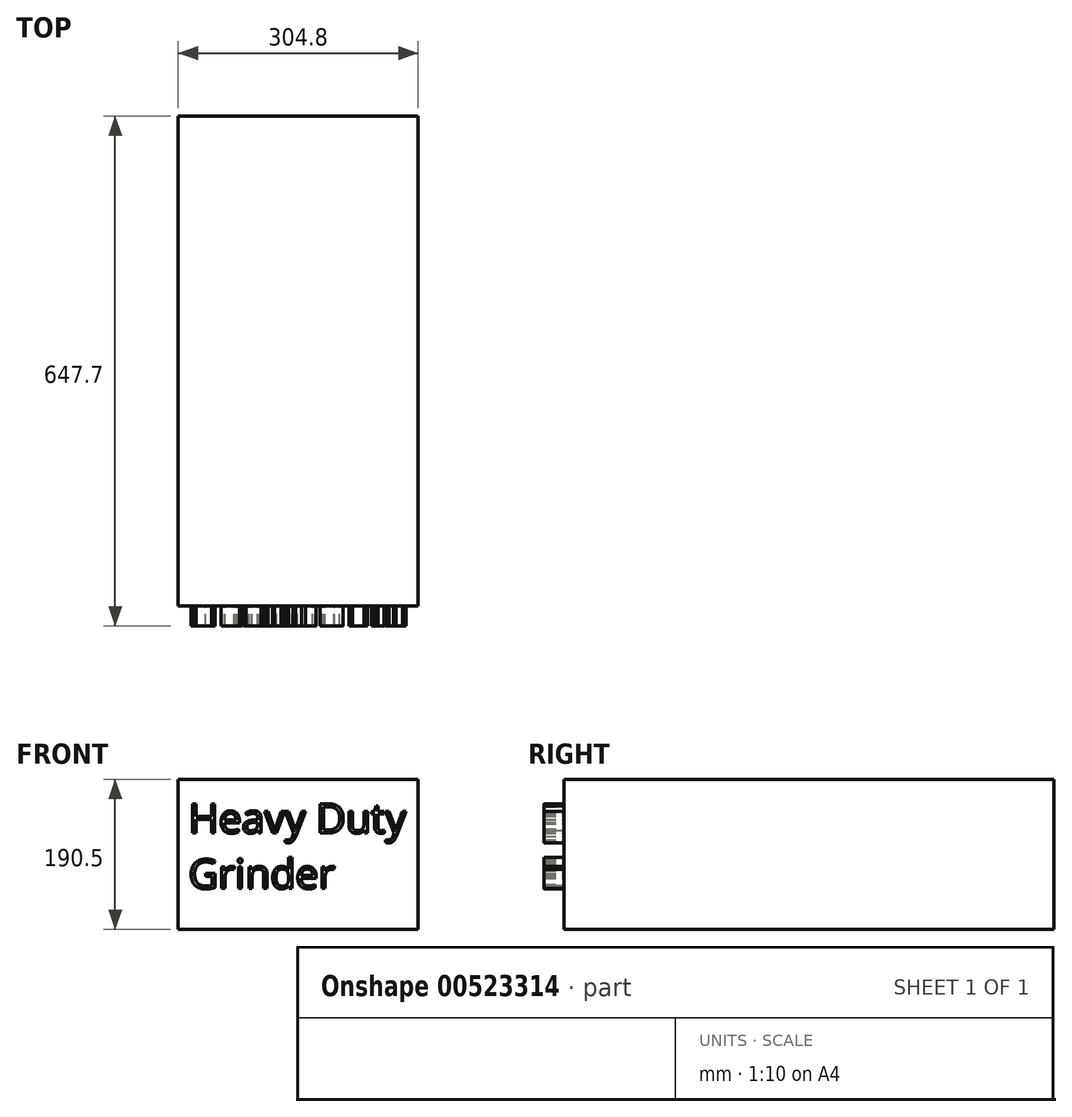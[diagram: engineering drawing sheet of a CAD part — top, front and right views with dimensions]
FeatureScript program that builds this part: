
annotation { "Feature Type Name" : "Feature", "Feature Type Description" : "" }
export const myFeature = defineFeature(function(context is Context, id is Id, definition is map)
    precondition{}
    {
        {
            var Q0;
            Q0=qCreatedBy(makeId("Front.planeOp"),FACE);
            var sketch = newSketch(context, id + "F0", { "sketchPlane" : qUnion([Q0])});
            skLineSegment(sketch, "E0.bottom", {"start": v(152.4, 95.25) * mm, "end": v(-152.4, 95.25) * mm});
            skLineSegment(sketch, "E0.top", {"start": v(152.4, -95.25) * mm, "end": v(-152.4, -95.25) * mm});
            skLineSegment(sketch, "E0.left", {"start": v(152.4, 95.25) * mm, "end": v(152.4, -95.25) * mm});
            skLineSegment(sketch, "E0.right", {"start": v(-152.4, 95.25) * mm, "end": v(-152.4, -95.25) * mm});
            skPoint(sketch, "E0.middle", {"position": v(0, 0) * mm});
            skSolve(sketch);
        }
        {
            var Q0;
            Q0=makeQuery(id+"F0.imprint","IMPRINT",FACE,{"disambiguationData":[TD([[makeQuery(id+"F0.imprint","IMPRINT",EDGE,{"derivedFrom":sQuery(id+"F0.wireOp",EDGE,"E0.bottom")}),1.0]])]});
            extrude(context, id + "F1", {"entities" : qUnion([Q0]), "depth" : 622.3 * mm, "offsetDistance" : 25.4 * mm});
        }
        {
            var Q0;
            Q0=makeQuery(id+"F1.opExtrude","CAP_FACE",FACE,{"disambiguationData":[OSD([sQuery(id+"F0.wireOp",EDGE,"E0.bottom"),sQuery(id+"F0.wireOp",EDGE,"E0.top"),sQuery(id+"F0.wireOp",EDGE,"E0.left"),sQuery(id+"F0.wireOp",EDGE,"E0.right")])],"isStart":false});
            var sketch = newSketch(context, id + "F2", { "sketchPlane" : qUnion([Q0])});
            skText(sketch, "E1", { "text": "Heavy Duty \nGrinder", "fontName": "OpenSans-Regular.ttf"});
            const initialGuessF2  = {"E1": [-0.13926, 0.0272, 1, 0, 0.03737]};
            skSetInitialGuess(sketch, initialGuessF2);
            skSolve(sketch);
        }
        {
            var Q0;
            Q0 = qSketchRegion(id + "F2", true);
            extrude(context, id + "F3", {"entities" : qUnion([Q0]), "operationType" : NewBodyOperationType.ADD, "depth" : 25.4 * mm, "offsetDistance" : 25.4 * mm});
        }
    });
